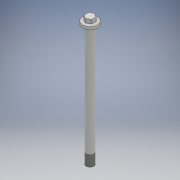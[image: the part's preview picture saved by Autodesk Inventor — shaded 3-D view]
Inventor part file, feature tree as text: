
AUTODESK INVENTOR PART (.ipt)
format: ipt  version: 2018 (Build 220112000, 112)  size: 110,592 bytes
history: native  units: mm
features: extrude x3, sketch x3, other x1, thread x1
ambient origin geometry x8: Origin, YZ Plane, XZ Plane, XY Plane, X Axis, Y Axis, Z Axis, Center Point
bodies: Body1 (feature_tree)
feature tree (8):
  other  "ソリッド1"
  extrude  "押し出し1"  Depth=11.9mm
  thread  "ねじ1"
  extrude  "押し出し2"  Depth=188.0mm TaperAngle=0.0deg
  extrude  "押し出し3"  Depth=17.0mm TaperAngle=0.0deg
  sketch  "スケッチ1"
  sketch  "スケッチ3"
  sketch  "スケッチ4"
